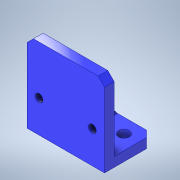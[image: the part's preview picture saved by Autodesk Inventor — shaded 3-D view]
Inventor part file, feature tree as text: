
AUTODESK INVENTOR PART (.ipt)
format: ipt  version: 2022.6 (Build 266554000, 554)  size: 185,856 bytes
history: native  units: mm
features: sketch x7, extrude x4, plane x2, hole x2, projected_geometry x2, chamfer x1, rib x1
ambient origin geometry x8: Origin, YZ Plane, XZ Plane, XY Plane, X Axis, Y Axis, Z Axis, Center Point
bodies: Solid1 (feature_tree)
feature tree (19):
  extrude  "Extrusion1"  Depth=20.0mm
  plane  "Work Plane1"
  plane  "Work Plane2"
  sketch  "Sketch2"  dims[d2=3.0mm d3=0.0mm d9=12.0mm d10=23.0mm]
  extrude  "Extrusion4"  Depth=12.0mm
  extrude  "Extrusion5"  Depth=24.0mm
  hole  "Hole3"  [1 undecoded]
  chamfer  "Chamfer1"  Distance=15.0mm
  rib  "Rib1"
  sketch  "Sketch11"  dims[d57=3.4mm d58=6.0mm d59=4.0mm d60=2.0mm d61=90.0deg d62=8.0mm d63=20.594885mm d65=2.0mm d66=2.0mm d67=45.0deg d75=1.0mm d76=2.0mm d77=0.0mm d78=0.0mm d79=1.0mm d80=1.0mm d87=15.0mm d88=2.4mm d89=15.0mm d91=16.5mm d92=4.0mm d93=3.0mm d94=0.0mm d95=5.0mm d96=2.0mm d97=2.4mm d98=6.0mm d99=6.5mm d100=1.3mm d101=90.0deg d102=8.0mm d103=20.594885mm]
  extrude  "Extrusion7"  Depth=15.0mm
  hole  "Hole4"  [1 undecoded]
  sketch  "Sketch1"  dims[d0=24.0mm d1=20.0mm]
  sketch  "Sketch5"  dims[d47=0.0mm d48=24.0mm]
  sketch  "Sketch6"  dims[d49=5.0mm d50=0.0mm d51=3.0mm d52=15.0mm d53=0.0mm]
  sketch  "Sketch7"  dims[d54=15.0mm d55=4.5mm]
  sketch  "Sketch10"  dims[d56=4.5mm]
  projected_geometry  "Projected Loop4"
  projected_geometry  "Projected Loop6"
note: 2 required parameter values undecoded (feature->parameter linkage not recoverable at this tier; creation-order binding heuristic only, values carry confidence <= 0.55)
